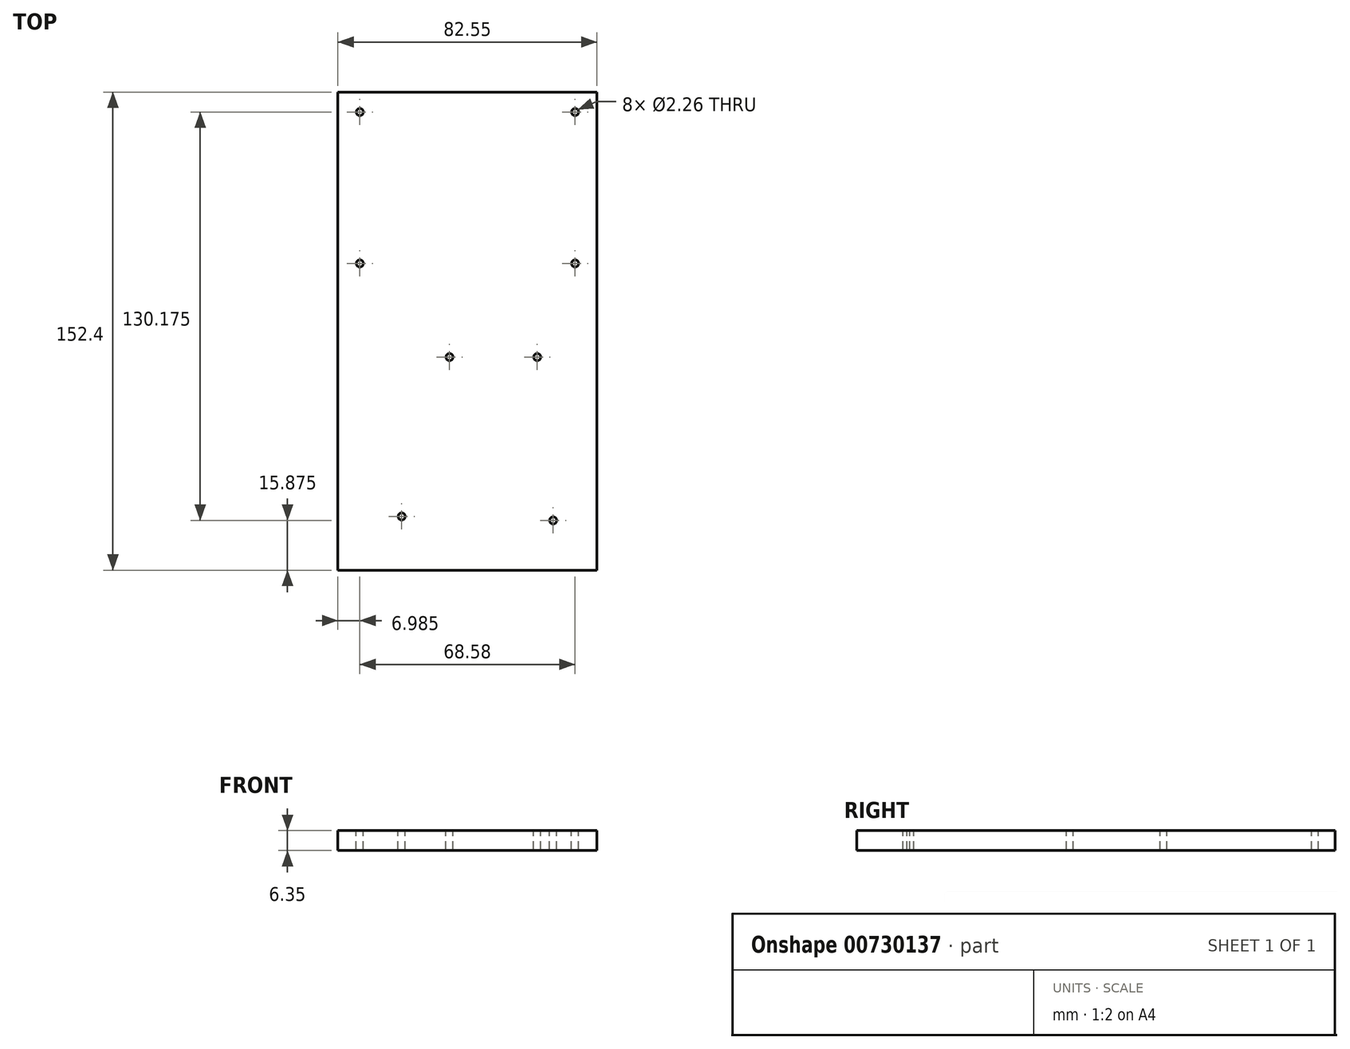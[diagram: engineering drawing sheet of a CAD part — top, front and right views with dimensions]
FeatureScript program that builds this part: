
annotation { "Feature Type Name" : "Feature", "Feature Type Description" : "" }
export const myFeature = defineFeature(function(context is Context, id is Id, definition is map)
    precondition{}
    {
        {
            var Q0;
            Q0=qCreatedBy(makeId("Top.planeOp"),FACE);
            var sketch = newSketch(context, id + "F0", { "sketchPlane" : qUnion([Q0])});
            skLineSegment(sketch, "E0", {"start": v(0, 0) * mm, "end": v(82.55, 0) * mm});
            skLineSegment(sketch, "E1", {"start": v(82.55, 0) * mm, "end": v(82.55, 152.4) * mm});
            skLineSegment(sketch, "E2", {"start": v(82.55, 152.4) * mm, "end": v(0, 152.4) * mm});
            skLineSegment(sketch, "E3", {"start": v(0, 152.4) * mm, "end": v(0, 0) * mm});
            skPoint(sketch, "E4.visualSharp", {"position": v(0, 152.4) * mm});
            skPoint(sketch, "E5.visualSharp", {"position": v(82.55, 152.4) * mm});
            skPoint(sketch, "E6.visualSharp", {"position": v(82.55, 0) * mm});
            skPoint(sketch, "E7.visualSharp", {"position": v(0, 0) * mm});
            skSolve(sketch);
        }
        {
            var Q0;
            Q0=qSketchRegion(id+"F0",true);
            extrude(context, id + "F1", {"entities" : qUnion([Q0]), "depth" : 6.35 * mm, "offsetDistance" : 25.4 * mm});
        }
        {
            var Q0;
            Q0=qCreatedBy(makeId("Top.planeOp"),FACE);
            var sketch = newSketch(context, id + "F2", { "sketchPlane" : qUnion([Q0])});
            skPoint(sketch, "E8", {"position": v(75.57, 97.8) * mm});
            skPoint(sketch, "E9", {"position": v(6.98, 97.8) * mm});
            skPoint(sketch, "E10", {"position": v(6.98, 146.05) * mm});
            skPoint(sketch, "E11", {"position": v(75.57, 146.05) * mm});
            skPoint(sketch, "E12", {"position": v(20.32, 17.14) * mm});
            skPoint(sketch, "E13", {"position": v(68.58, 15.88) * mm});
            skPoint(sketch, "E14", {"position": v(63.5, 67.95) * mm});
            skPoint(sketch, "E15", {"position": v(35.56, 67.95) * mm});
            skSolve(sketch);
        }
        {
            var Q0;
            Q0=sQuery(id+"F2.wireOp",VERTEX,"E9");
            var Q1;
            Q1=sQuery(id+"F2.wireOp",VERTEX,"E10");
            var Q2;
            Q2=sQuery(id+"F2.wireOp",VERTEX,"E11");
            var Q3;
            Q3=sQuery(id+"F2.wireOp",VERTEX,"E8");
            var Q4;
            Q4=sQuery(id+"F2.wireOp",VERTEX,"E15");
            var Q5;
            Q5=sQuery(id+"F2.wireOp",VERTEX,"E14");
            var Q6;
            Q6=sQuery(id+"F2.wireOp",VERTEX,"E12");
            var Q7;
            Q7=sQuery(id+"F2.wireOp",VERTEX,"E13");
            var Q8;
            Q8=makeQuery(id+"F1.opExtrude","SWEPT_BODY",BODY,{"disambiguationData":[OSD([sQuery(id+"F0.wireOp",EDGE,"E0"),sQuery(id+"F0.wireOp",EDGE,"E1"),sQuery(id+"F0.wireOp",EDGE,"OE1n4c4a-sDVM-iTu2-7ck2-WDPZia7Jgp9O"),sQuery(id+"F0.wireOp",EDGE,"pvwuTijB-Xi52-23gZ-Y7J5-U1gqpMojkoq3"),sQuery(id+"F0.wireOp",EDGE,"SHHxBChA-lvkI-lRBh-ukSY-QTbABry1Lqso"),sQuery(id+"F0.wireOp",EDGE,"CPgoxdOC-QvgX-zmgb-s01C-n2swE1ywNPbG"),sQuery(id+"F0.wireOp",EDGE,"E2"),sQuery(id+"F0.wireOp",EDGE,"E3")])]});
            hole(context, id + "F3", {"style" : HoleStyle.SIMPLE, "endStyle" : HoleEndStyle.THROUGH, "oppositeDirection" : true, "standardTappedOrClearance" : lookupTablePath({ "standard" : "ANSI", "engagement" : "75%", "pitch" : "40 tpi", "size" : "#4", "type" : "Tapped" }), "standardBlindInLast" : lookupTablePath({ "standard" : "ANSI", "engagement" : "75%", "pitch" : "40 tpi", "size" : "#4", "type" : "Tapped" }), "holeDiameter" : 2.26 * mm, "majorDiameter" : 2.84 * mm, "showTappedDepth" : true, "isTappedThrough" : true, "tappedDepth" : 13.97 * mm, "tapClearance" : 5, "startFromSketch" : true, "locations" : qUnion([Q0, Q1, Q2, Q3, Q4, Q5, Q6, Q7]), "scope" : qUnion([Q8])});
        }
    });
